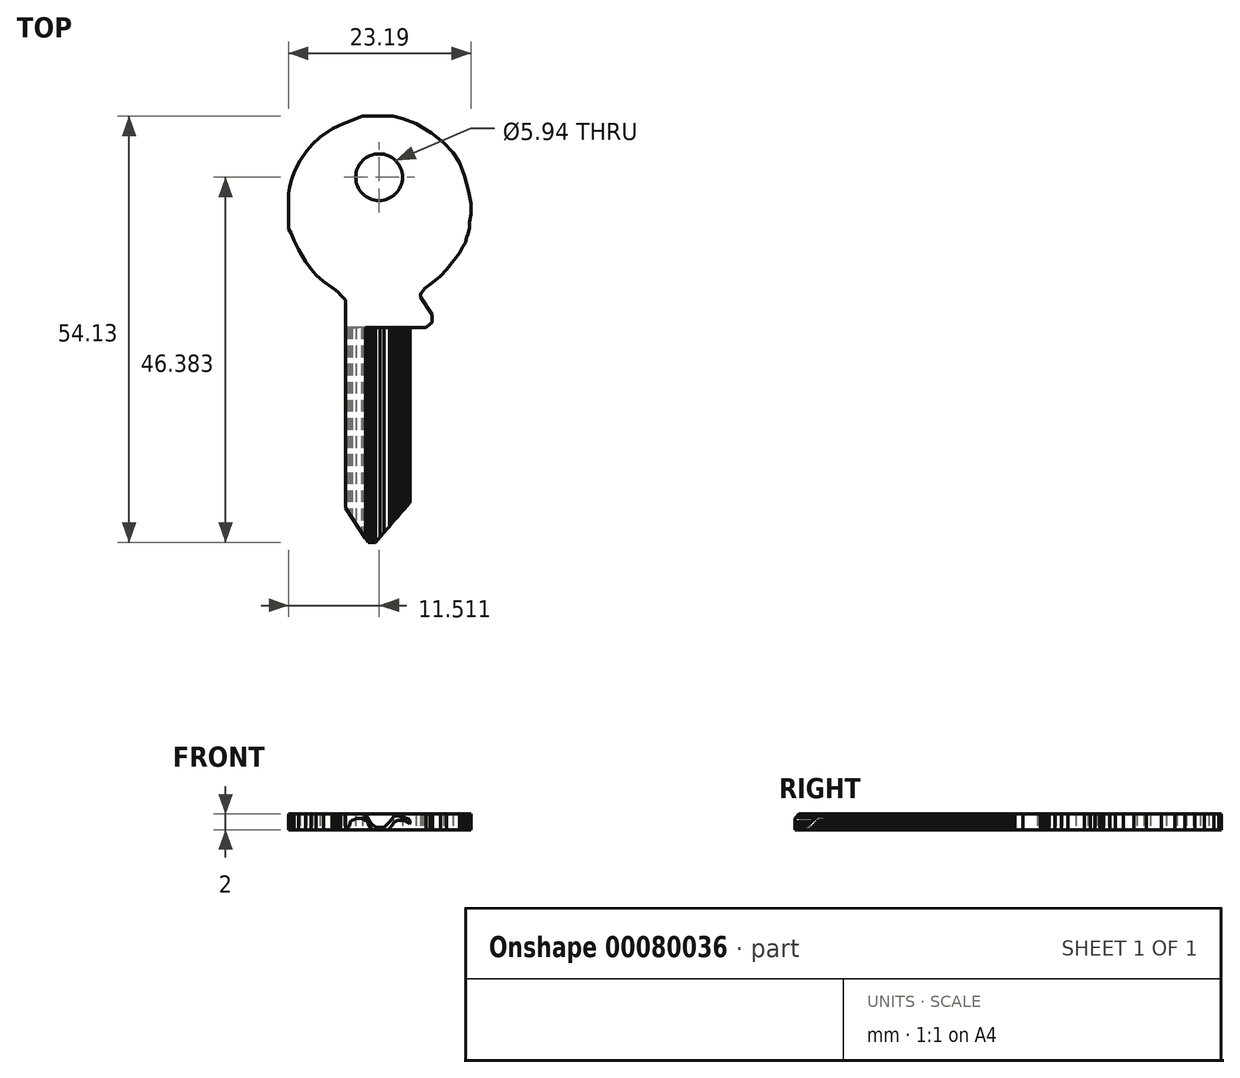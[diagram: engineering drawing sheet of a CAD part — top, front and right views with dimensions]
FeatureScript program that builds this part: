
annotation { "Feature Type Name" : "Feature", "Feature Type Description" : "" }
export const myFeature = defineFeature(function(context is Context, id is Id, definition is map)
    precondition{}
    {
        {
            var Q0;
            Q0=qCreatedBy(makeId("Top.planeOp"),FACE);
            var sketch = newSketch(context, id + "F0", { "sketchPlane" : qUnion([Q0])});
            skLineSegment(sketch, "E0", {"start": v(16.78, -50.08) * mm, "end": v(12.36, -55.21) * mm});
            skLineSegment(sketch, "E1", {"start": v(12.36, -55.21) * mm, "end": v(11.8, -55.21) * mm});
            skLineSegment(sketch, "E2", {"start": v(11.8, -55.21) * mm, "end": v(11.43, -55.21) * mm});
            skLineSegment(sketch, "E3", {"start": v(11.43, -55.21) * mm, "end": v(11.02, -54.66) * mm});
            skLineSegment(sketch, "E4", {"start": v(11.02, -54.66) * mm, "end": v(8.53, -50.82) * mm});
            skLineSegment(sketch, "E5", {"start": v(8.53, -50.82) * mm, "end": v(8.53, -25.29) * mm});
            skLineSegment(sketch, "E6", {"start": v(8.53, -25.29) * mm, "end": v(8.53, -24.84) * mm});
            skLineSegment(sketch, "E7", {"start": v(8.53, -24.84) * mm, "end": v(8.53, -24.42) * mm});
            skLineSegment(sketch, "E8", {"start": v(8.53, -24.42) * mm, "end": v(8.18, -24.06) * mm});
            skLineSegment(sketch, "E9", {"start": v(8.18, -24.06) * mm, "end": v(7.9, -23.8) * mm});
            skLineSegment(sketch, "E10", {"start": v(7.9, -23.8) * mm, "end": v(7.65, -23.5) * mm});
            skLineSegment(sketch, "E11", {"start": v(7.65, -23.5) * mm, "end": v(7.28, -23.17) * mm});
            skLineSegment(sketch, "E12", {"start": v(7.28, -23.17) * mm, "end": v(6.86, -22.85) * mm});
            skLineSegment(sketch, "E13", {"start": v(6.86, -22.85) * mm, "end": v(5.77, -22.08) * mm});
            skLineSegment(sketch, "E14", {"start": v(5.77, -22.08) * mm, "end": v(4.79, -21.27) * mm});
            skLineSegment(sketch, "E15", {"start": v(4.79, -21.27) * mm, "end": v(4.16, -20.5) * mm});
            skLineSegment(sketch, "E16", {"start": v(4.16, -20.5) * mm, "end": v(3.49, -19.52) * mm});
            skLineSegment(sketch, "E17", {"start": v(3.49, -19.52) * mm, "end": v(2.61, -18.04) * mm});
            skLineSegment(sketch, "E18", {"start": v(2.61, -18.04) * mm, "end": v(2.01, -16.85) * mm});
            skLineSegment(sketch, "E19", {"start": v(2.01, -16.85) * mm, "end": v(1.63, -15.93) * mm});
            skLineSegment(sketch, "E20", {"start": v(1.63, -15.93) * mm, "end": v(1.31, -15.4) * mm});
            skLineSegment(sketch, "E21", {"start": v(1.31, -15.4) * mm, "end": v(1.31, -11.64) * mm});
            skLineSegment(sketch, "E22", {"start": v(1.31, -11.64) * mm, "end": v(1.31, -10.9) * mm});
            skLineSegment(sketch, "E23", {"start": v(1.31, -10.9) * mm, "end": v(1.43, -10.08) * mm});
            skLineSegment(sketch, "E24", {"start": v(1.43, -10.08) * mm, "end": v(1.72, -9.15) * mm});
            skLineSegment(sketch, "E25", {"start": v(1.72, -9.15) * mm, "end": v(2.06, -8.07) * mm});
            skLineSegment(sketch, "E26", {"start": v(2.06, -8.07) * mm, "end": v(2.8, -6.7) * mm});
            skLineSegment(sketch, "E27", {"start": v(2.8, -6.7) * mm, "end": v(3.58, -5.5) * mm});
            skLineSegment(sketch, "E28", {"start": v(3.58, -5.5) * mm, "end": v(4.37, -4.6) * mm});
            skLineSegment(sketch, "E29", {"start": v(4.37, -4.6) * mm, "end": v(5.33, -3.71) * mm});
            skLineSegment(sketch, "E30", {"start": v(5.33, -3.71) * mm, "end": v(6.93, -2.63) * mm});
            skLineSegment(sketch, "E31", {"start": v(6.93, -2.63) * mm, "end": v(8.27, -2) * mm});
            skLineSegment(sketch, "E32", {"start": v(8.27, -2) * mm, "end": v(9.76, -1.44) * mm});
            skLineSegment(sketch, "E33", {"start": v(9.76, -1.44) * mm, "end": v(10.72, -1.08) * mm});
            skLineSegment(sketch, "E34", {"start": v(10.72, -1.08) * mm, "end": v(14.6, -1.08) * mm});
            skLineSegment(sketch, "E35", {"start": v(14.6, -1.08) * mm, "end": v(15.79, -1.37) * mm});
            skLineSegment(sketch, "E36", {"start": v(15.79, -1.37) * mm, "end": v(17.54, -2.04) * mm});
            skLineSegment(sketch, "E37", {"start": v(17.54, -2.04) * mm, "end": v(19.51, -3.2) * mm});
            skLineSegment(sketch, "E38", {"start": v(19.51, -3.2) * mm, "end": v(21, -4.46) * mm});
            skLineSegment(sketch, "E39", {"start": v(21, -4.46) * mm, "end": v(22.19, -5.72) * mm});
            skLineSegment(sketch, "E40", {"start": v(22.19, -5.72) * mm, "end": v(23, -6.99) * mm});
            skLineSegment(sketch, "E41", {"start": v(23, -6.99) * mm, "end": v(23.68, -8.66) * mm});
            skLineSegment(sketch, "E42", {"start": v(23.68, -8.66) * mm, "end": v(24.16, -10.6) * mm});
            skLineSegment(sketch, "E43", {"start": v(24.16, -10.6) * mm, "end": v(24.5, -12.2) * mm});
            skLineSegment(sketch, "E44", {"start": v(24.5, -12.2) * mm, "end": v(24.5, -13.5) * mm});
            skLineSegment(sketch, "E45", {"start": v(24.5, -13.5) * mm, "end": v(24.31, -14.54) * mm});
            skLineSegment(sketch, "E46", {"start": v(24.31, -14.54) * mm, "end": v(24.31, -15.24) * mm});
            skLineSegment(sketch, "E47", {"start": v(24.31, -15.24) * mm, "end": v(24.11, -16.07) * mm});
            skLineSegment(sketch, "E48", {"start": v(24.11, -16.07) * mm, "end": v(23.95, -16.47) * mm});
            skLineSegment(sketch, "E49", {"start": v(23.95, -16.47) * mm, "end": v(23.78, -17.14) * mm});
            skLineSegment(sketch, "E50", {"start": v(23.78, -17.14) * mm, "end": v(23.38, -17.72) * mm});
            skLineSegment(sketch, "E51", {"start": v(23.38, -17.72) * mm, "end": v(23.05, -18.48) * mm});
            skLineSegment(sketch, "E52", {"start": v(23.05, -18.48) * mm, "end": v(22.34, -19.37) * mm});
            skLineSegment(sketch, "E53", {"start": v(22.34, -19.37) * mm, "end": v(21.4, -20.56) * mm});
            skLineSegment(sketch, "E54", {"start": v(21.4, -20.56) * mm, "end": v(20.6, -21.38) * mm});
            skLineSegment(sketch, "E55", {"start": v(20.6, -21.38) * mm, "end": v(19.6, -22.21) * mm});
            skLineSegment(sketch, "E56", {"start": v(19.6, -22.21) * mm, "end": v(18.58, -22.94) * mm});
            skLineSegment(sketch, "E57", {"start": v(18.58, -22.94) * mm, "end": v(18.35, -23.32) * mm});
            skLineSegment(sketch, "E58", {"start": v(18.35, -23.32) * mm, "end": v(18.14, -23.55) * mm});
            skLineSegment(sketch, "E59", {"start": v(18.14, -23.55) * mm, "end": v(18.1, -23.74) * mm});
            skLineSegment(sketch, "E60", {"start": v(18.1, -23.74) * mm, "end": v(18.1, -24.05) * mm});
            skLineSegment(sketch, "E61", {"start": v(18.1, -24.05) * mm, "end": v(19.54, -26.29) * mm});
            skLineSegment(sketch, "E62", {"start": v(19.54, -26.29) * mm, "end": v(19.54, -26.72) * mm});
            skLineSegment(sketch, "E63", {"start": v(19.54, -26.72) * mm, "end": v(19.54, -27) * mm});
            skLineSegment(sketch, "E64", {"start": v(19.54, -27) * mm, "end": v(19.54, -27.27) * mm});
            skLineSegment(sketch, "E65", {"start": v(19.54, -27.27) * mm, "end": v(19.29, -27.5) * mm});
            skLineSegment(sketch, "E66", {"start": v(19.29, -27.5) * mm, "end": v(18.8, -27.91) * mm});
            skLineSegment(sketch, "E67", {"start": v(18.8, -27.91) * mm, "end": v(16.78, -27.91) * mm});
            skLineSegment(sketch, "E68", {"start": v(16.78, -27.91) * mm, "end": v(16.78, -50.08) * mm});
            skCircle(sketch, "E69", {"center": v(12.82, -8.83) * mm, "radius": 2.97 * mm});
            skSolve(sketch);
        }
        {
            var Q0;
            Q0 = qSketchRegion(id + "F0", true);
            extrude(context, id + "F1", {"entities" : qUnion([Q0]), "endBound" : BoundingType.SYMMETRIC, "depth" : 2 * mm});
        }
        {
            var Q0;
            Q0=makeQuery(id+"F1.opExtrude","SWEPT_FACE",FACE,{"disambiguationData":[OSD([sQuery(id+"F0.wireOp",EDGE,"E1"),sQuery(id+"F0.wireOp",EDGE,"E2")])]});
            cPlane(context, id + "F2", {"entities" : qUnion([Q0]), "cplaneType" : CPlaneType.OFFSET, "offset" : 0 * mm, "width" : 150 * mm, "height" : 150 * mm});
        }
        {
            var Q0;
            Q0=qCreatedBy(id+"F2.planeOp",FACE);
            var sketch = newSketch(context, id + "F3", { "sketchPlane" : qUnion([Q0])});
            skLineSegment(sketch, "E70", {"start": v(8.53, 1) * mm, "end": v(11.08, 1) * mm});
            skLineSegment(sketch, "E71", {"start": v(11.08, 1) * mm, "end": v(11.37, 0.54) * mm});
            skLineSegment(sketch, "E72", {"start": v(11.37, 0.54) * mm, "end": v(11.66, 0.01) * mm});
            skLineSegment(sketch, "E73", {"start": v(11.66, 0.01) * mm, "end": v(11.92, -0.33) * mm});
            skLineSegment(sketch, "E74", {"start": v(11.92, -0.33) * mm, "end": v(12.36, -0.62) * mm});
            skLineSegment(sketch, "E75", {"start": v(12.36, -0.62) * mm, "end": v(12.93, -0.71) * mm});
            skLineSegment(sketch, "E76", {"start": v(12.93, -0.71) * mm, "end": v(13.46, -0.71) * mm});
            skLineSegment(sketch, "E77", {"start": v(13.46, -0.71) * mm, "end": v(13.8, -0.36) * mm});
            skLineSegment(sketch, "E78", {"start": v(13.8, -0.36) * mm, "end": v(14.12, -0.04) * mm});
            skLineSegment(sketch, "E79", {"start": v(14.12, -0.04) * mm, "end": v(14.41, 0.28) * mm});
            skLineSegment(sketch, "E80", {"start": v(14.41, 0.28) * mm, "end": v(14.67, 0.6) * mm});
            skLineSegment(sketch, "E81", {"start": v(14.67, 0.6) * mm, "end": v(14.8, 0.72) * mm});
            skLineSegment(sketch, "E82", {"start": v(14.8, 0.72) * mm, "end": v(15.15, 0.72) * mm});
            skLineSegment(sketch, "E83", {"start": v(15.15, 0.72) * mm, "end": v(15.61, 0.63) * mm});
            skLineSegment(sketch, "E84", {"start": v(15.61, 0.63) * mm, "end": v(16.02, 0.54) * mm});
            skLineSegment(sketch, "E85", {"start": v(16.02, 0.54) * mm, "end": v(16.35, 0.42) * mm});
            skLineSegment(sketch, "E86", {"start": v(16.35, 0.42) * mm, "end": v(16.68, 0.33) * mm});
            skLineSegment(sketch, "E87", {"start": v(16.68, 0.33) * mm, "end": v(16.8, -0.21) * mm});
            skLineSegment(sketch, "E88", {"start": v(16.8, -0.21) * mm, "end": v(16.68, -0.24) * mm});
            skLineSegment(sketch, "E89", {"start": v(16.68, -0.24) * mm, "end": v(16.48, -0.1) * mm});
            skLineSegment(sketch, "E90", {"start": v(16.48, -0.1) * mm, "end": v(16.22, 0.05) * mm});
            skLineSegment(sketch, "E91", {"start": v(16.22, 0.05) * mm, "end": v(15.9, 0.18) * mm});
            skLineSegment(sketch, "E92", {"start": v(15.9, 0.18) * mm, "end": v(15.59, 0.18) * mm});
            skLineSegment(sketch, "E93", {"start": v(15.59, 0.18) * mm, "end": v(15.13, 0.18) * mm});
            skLineSegment(sketch, "E94", {"start": v(15.13, 0.18) * mm, "end": v(14.93, 0.07) * mm});
            skLineSegment(sketch, "E95", {"start": v(14.93, 0.07) * mm, "end": v(14.7, -0.04) * mm});
            skLineSegment(sketch, "E96", {"start": v(14.7, -0.04) * mm, "end": v(14.57, -0.25) * mm});
            skLineSegment(sketch, "E97", {"start": v(14.57, -0.25) * mm, "end": v(14.37, -0.5) * mm});
            skLineSegment(sketch, "E98", {"start": v(14.37, -0.5) * mm, "end": v(14.22, -0.75) * mm});
            skLineSegment(sketch, "E99", {"start": v(14.22, -0.75) * mm, "end": v(14.05, -0.96) * mm});
            skLineSegment(sketch, "E100", {"start": v(14.05, -0.96) * mm, "end": v(13.92, -1.05) * mm});
            skLineSegment(sketch, "E101", {"start": v(13.92, -1.05) * mm, "end": v(11.94, -1.05) * mm});
            skLineSegment(sketch, "E102", {"start": v(11.94, -1.05) * mm, "end": v(11.6, -0.54) * mm});
            skLineSegment(sketch, "E103", {"start": v(11.6, -0.54) * mm, "end": v(11.26, 0.08) * mm});
            skLineSegment(sketch, "E104", {"start": v(11.26, 0.08) * mm, "end": v(10.86, 0.3) * mm});
            skLineSegment(sketch, "E105", {"start": v(10.86, 0.3) * mm, "end": v(10.56, 0.46) * mm});
            skLineSegment(sketch, "E106", {"start": v(10.56, 0.46) * mm, "end": v(10.23, 0.46) * mm});
            skLineSegment(sketch, "E107", {"start": v(10.23, 0.46) * mm, "end": v(9.9, 0.46) * mm});
            skLineSegment(sketch, "E108", {"start": v(9.9, 0.46) * mm, "end": v(9.67, 0.33) * mm});
            skLineSegment(sketch, "E109", {"start": v(9.67, 0.33) * mm, "end": v(9.39, 0.18) * mm});
            skLineSegment(sketch, "E110", {"start": v(9.39, 0.18) * mm, "end": v(9.15, 0) * mm});
            skLineSegment(sketch, "E111", {"start": v(9.15, 0) * mm, "end": v(9.15, -0.23) * mm});
            skLineSegment(sketch, "E112", {"start": v(9.15, -0.23) * mm, "end": v(9, -0.56) * mm});
            skLineSegment(sketch, "E113", {"start": v(9, -0.56) * mm, "end": v(8.84, -0.78) * mm});
            skLineSegment(sketch, "E114", {"start": v(8.84, -0.78) * mm, "end": v(8.84, -0.99) * mm});
            skLineSegment(sketch, "E115", {"start": v(8.84, -0.99) * mm, "end": v(8.64, -1) * mm});
            skLineSegment(sketch, "E116", {"start": v(8.64, -1) * mm, "end": v(8.46, -1) * mm});
            skLineSegment(sketch, "E117", {"start": v(8.46, -1) * mm, "end": v(8.53, 1) * mm});
            skLineSegment(sketch, "E118", {"start": v(7.4, 1.61) * mm, "end": v(17.26, 1.61) * mm});
            skLineSegment(sketch, "E119", {"start": v(17.26, 1.61) * mm, "end": v(17.26, -2.4) * mm});
            skLineSegment(sketch, "E120", {"start": v(17.26, -2.4) * mm, "end": v(7.24, -2.4) * mm});
            skLineSegment(sketch, "E121", {"start": v(7.24, -2.4) * mm, "end": v(7.4, 1.61) * mm});
            skSolve(sketch);
        }
        {
            var Q0;
            Q0 = qSketchRegion(id + "F3", true);
            extrude(context, id + "F4", {"entities" : qUnion([Q0]), "operationType" : NewBodyOperationType.REMOVE, "oppositeDirection" : true, "depth" : 27.3 * mm});
        }
    });
